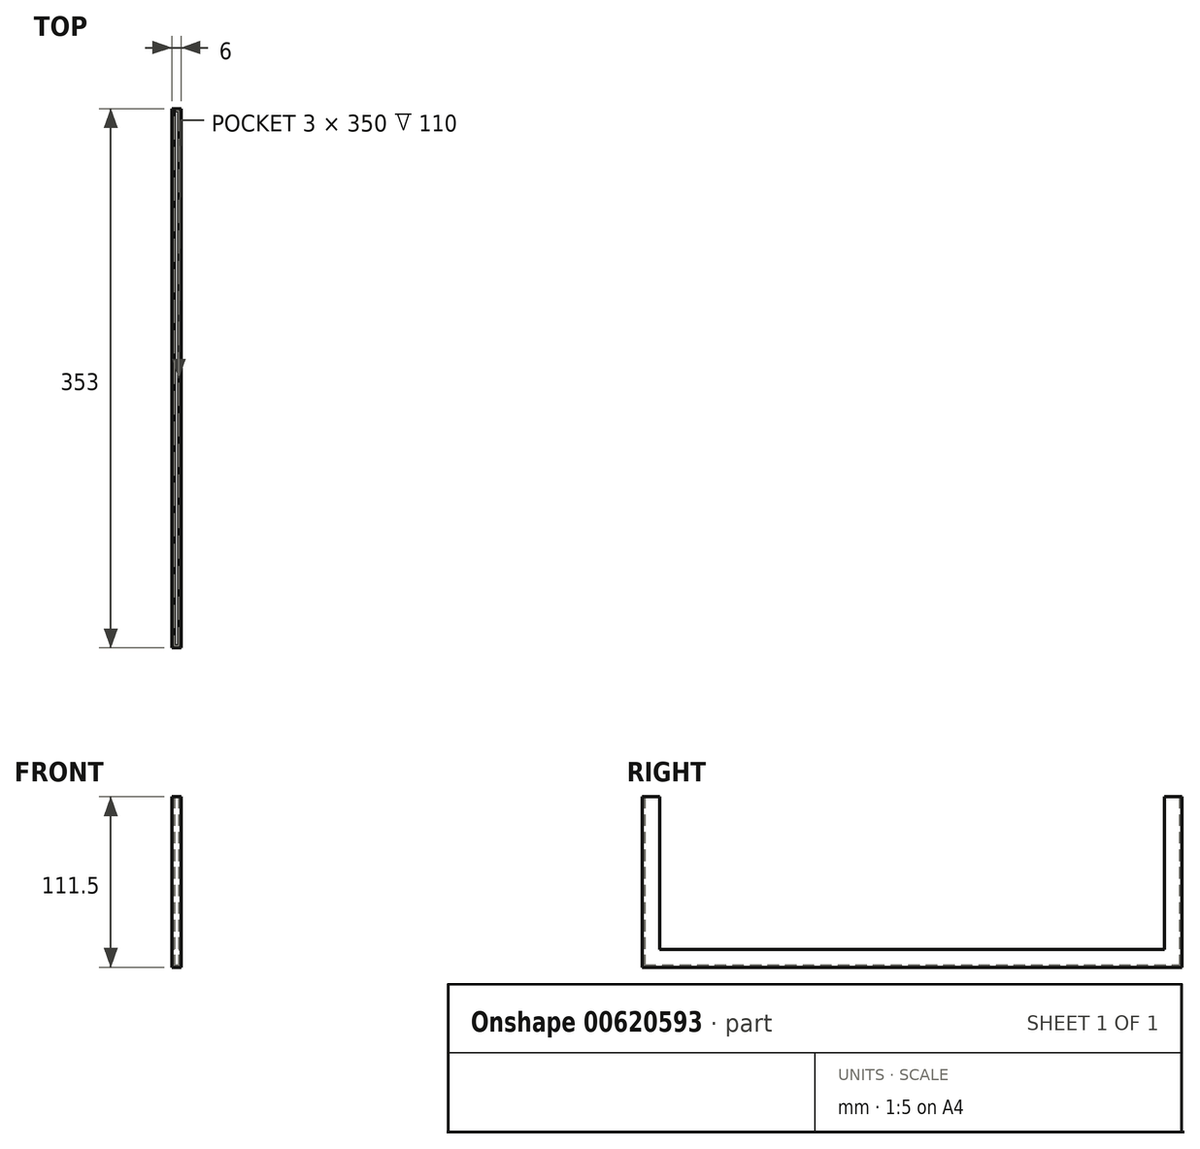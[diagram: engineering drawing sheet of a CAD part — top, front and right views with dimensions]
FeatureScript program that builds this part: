
annotation { "Feature Type Name" : "Feature", "Feature Type Description" : "" }
export const myFeature = defineFeature(function(context is Context, id is Id, definition is map)
    precondition{}
    {
        {
            var Q0;
            Q0=qCreatedBy(makeId("Top.planeOp"),FACE);
            var sketch = newSketch(context, id + "F0", { "sketchPlane" : qUnion([Q0])});
            skLineSegment(sketch, "E0.bottom", {"start": v(-3, -176.5) * mm, "end": v(3, -176.5) * mm});
            skLineSegment(sketch, "E0.top", {"start": v(-3, 176.5) * mm, "end": v(3, 176.5) * mm});
            skLineSegment(sketch, "E0.left", {"start": v(-3, -176.5) * mm, "end": v(-3, 176.5) * mm});
            skLineSegment(sketch, "E0.right", {"start": v(3, -176.5) * mm, "end": v(3, 176.5) * mm});
            skPoint(sketch, "E0.middle", {"position": v(0, 0) * mm});
            skSolve(sketch);
        }
        {
            var Q0;
            Q0 = qSketchRegion(id + "F0", true);
            extrude(context, id + "F1", {"entities" : qUnion([Q0]), "depth" : 1.5 * mm, "offsetDistance" : 25 * mm});
        }
        {
            var Q0;
            Q0=makeQuery(id+"F1.opExtrude","CAP_FACE",FACE,{"disambiguationData":[OSD([sQuery(id+"F0.wireOp",EDGE,"E0.bottom"),sQuery(id+"F0.wireOp",EDGE,"E0.top"),sQuery(id+"F0.wireOp",EDGE,"E0.left"),sQuery(id+"F0.wireOp",EDGE,"E0.right")])],"isStart":false});
            var sketch = newSketch(context, id + "F2", { "sketchPlane" : qUnion([Q0])});
            skLineSegment(sketch, "E1.0", {"start": v(1.5, 175) * mm, "end": v(-1.5, 175) * mm});
            skLineSegment(sketch, "E1.1", {"start": v(1.5, -175) * mm, "end": v(1.5, 175) * mm});
            skLineSegment(sketch, "E1.2", {"start": v(-1.5, -175) * mm, "end": v(1.5, -175) * mm});
            skLineSegment(sketch, "E1.3", {"start": v(-1.5, 175) * mm, "end": v(-1.5, -175) * mm});
            skSolve(sketch);
        }
        {
            var Q0;
            Q0=makeQuery(id+"F2.imprint","IMPRINT",FACE,{"disambiguationData":[TD([[makeQuery(id+"F2.imprint","IMPRINT",EDGE,{"derivedFrom":sQuery(id+"F2.wireOp",EDGE,"E1.0")}),-1.0]])]});
            extrude(context, id + "F3", {"entities" : qUnion([Q0]), "operationType" : NewBodyOperationType.ADD, "depth" : 10 * mm, "offsetDistance" : 25 * mm});
        }
        {
            var Q0;
            Q0=makeQuery(id+"F3.opExtrude","CAP_FACE",FACE,{"disambiguationData":[OSD([sQuery(id+"F0.wireOp",EDGE,"E0.bottom"),sQuery(id+"F0.wireOp",EDGE,"E0.top"),sQuery(id+"F0.wireOp",EDGE,"E0.left"),sQuery(id+"F0.wireOp",EDGE,"E0.right"),sQuery(id+"F2.wireOp",EDGE,"E1.0"),sQuery(id+"F2.wireOp",EDGE,"E1.1"),sQuery(id+"F2.wireOp",EDGE,"E1.2"),sQuery(id+"F2.wireOp",EDGE,"E1.3")])],"isStart":false});
            var sketch = newSketch(context, id + "F4", { "sketchPlane" : qUnion([Q0])});
            skLineSegment(sketch, "E2", {"start": v(-1.5, -175) * mm, "end": v(-1.5, -165) * mm});
            skLineSegment(sketch, "E3", {"start": v(-1.5, -165) * mm, "end": v(-3, -165) * mm});
            skLineSegment(sketch, "E4", {"start": v(1.5, -165) * mm, "end": v(3, -165) * mm});
            skLineSegment(sketch, "E5", {"start": v(3, -165) * mm, "end": v(3, -176.5) * mm});
            skLineSegment(sketch, "E6", {"start": v(3, -176.5) * mm, "end": v(-3, -176.5) * mm});
            skLineSegment(sketch, "E7", {"start": v(-3, -176.5) * mm, "end": v(-3, -165) * mm});
            skLineSegment(sketch, "E8", {"start": v(1.5, -165) * mm, "end": v(1.5, -175) * mm});
            skLineSegment(sketch, "E9", {"start": v(1.5, -175) * mm, "end": v(-1.5, -175) * mm});
            skSolve(sketch);
        }
        {
            var Q0;
            Q0=makeQuery(id+"F4.imprint","IMPRINT",FACE,{"disambiguationData":[TD([[makeQuery(id+"F4.imprint","IMPRINT",EDGE,{"derivedFrom":sQuery(id+"F4.wireOp",EDGE,"E2")}),-1.0]])]});
            extrude(context, id + "F5", {"entities" : qUnion([Q0]), "operationType" : NewBodyOperationType.ADD, "depth" : 100 * mm, "offsetDistance" : 25 * mm});
        }
        {
            var Q0;
            {var subQ0=sQuery(id+"F0.wireOp",EDGE,"E0.right");Q0=makeQuery(id+"F5.boolean.opBoolean","MERGE",FACE,{"derivedFrom":[makeQuery(id+"F3.boolean.opBoolean","MERGE",FACE,{"derivedFrom":[makeQuery(id+"F1.opExtrude","SWEPT_FACE",FACE,{"disambiguationData":[OSD([subQ0])]}),makeQuery(id+"F3.opExtrude","SWEPT_FACE",FACE,{"disambiguationData":[OSD([subQ0])]})]}),makeQuery(id+"F5.opExtrude","SWEPT_FACE",FACE,{"disambiguationData":[OSD([sQuery(id+"F4.wireOp",EDGE,"E5")])]})]});}
            var sketch = newSketch(context, id + "F6", { "sketchPlane" : qUnion([Q0])});
            skLineSegment(sketch, "E10.bottom", {"start": v(0, 0) * mm, "end": v(228.87, 0) * mm});
            skLineSegment(sketch, "E10.top", {"start": v(0, 47.29) * mm, "end": v(228.87, 47.29) * mm});
            skLineSegment(sketch, "E10.left", {"start": v(0, 0) * mm, "end": v(0, 47.29) * mm});
            skLineSegment(sketch, "E10.right", {"start": v(228.87, 0) * mm, "end": v(228.87, 47.29) * mm});
            skSolve(sketch);
        }
        {
            var Q0;
            Q0 = qSketchRegion(id + "F6", true);
            extrude(context, id + "F7", {"entities" : qUnion([Q0]), "operationType" : NewBodyOperationType.REMOVE, "oppositeDirection" : true, "depth" : 25 * mm, "offsetDistance" : 25 * mm});
        }
        {
            var Q0;
            Q0=makeQuery(id+"F1.opExtrude","SWEPT_BODY",BODY,{"disambiguationData":[OSD([sQuery(id+"F0.wireOp",EDGE,"E0.bottom"),sQuery(id+"F0.wireOp",EDGE,"E0.top"),sQuery(id+"F0.wireOp",EDGE,"E0.left"),sQuery(id+"F0.wireOp",EDGE,"E0.right")])]});
            var Q1;
            Q1=qCreatedBy(makeId("Front.planeOp"),FACE);
            mirror(context, id + "F8", {"operationType" : NewBodyOperationType.ADD, "entities" : qUnion([Q0]), "mirrorPlane" : qUnion([Q1])});
        }
    });
